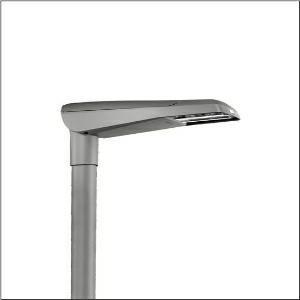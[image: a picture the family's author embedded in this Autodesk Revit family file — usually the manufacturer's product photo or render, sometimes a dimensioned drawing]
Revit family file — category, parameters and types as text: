
# Revit family: streetlight_sl_11_iq_micro___st1_2a_5xc1ac1f08de_2d80
name_source: partatom
category: Lighting Fixtures
units: mm (PartAtom-declared; Revit-internal decimal feet)

## family parameters
Cut with Voids When Loaded = No
Host = Face
Light Source = No
Part Type = Normal
Room Calculation Point = No
Round Connector Dimension = Use Diameter
Shared = No

## types (1)
- --- (1 x LED, 3860 lm, 27.4 W, 4000K)
    Apparent Load = 27 VA
    CIE Flux Codes = 33 71 96 100 100
    Color Rendering = 70
    Color Temperature = 4000K
    Default Elevation = 1800 mm
    Description = Streetlight SL 11 iQ micro, mast luminaire, primary light control with 3 zone facetted reflector, of plastic, silver coated, highly specular, primary optical cover: cover, of PMMA, transparent, light distribution: ST1.2a, light emission: direct distribution, primary light characteristic: asymmetric, installation type: post-top, side-entry, lamps: LED, High Power LED, rated values: 3.620lm | 27,7W | 130,7lm/W (begin service life); end service life: 3.620lm | 28,1W; at 50% lumin. flux: 1.810lm | 13,4W | 135,1lm/W, colour temperature: 2200/2700/3000/4000K, colour rendering: CRI > 70, light colour: 722/727/730/740, light setting 1 begin service life: 100% | 3.620lm | 27,7W | 130,7lm/W | 3.000K, light setting 1 end service life: 28,1W, further light settings possible, control: Street-Remote, Auto-Match, Temp-Guard, Lumen-Switch, Night-Set, Smart-Wire, Light-Fading, Desk-Remote (wireless, voltage-free reading and setting of iQ features in the workshop via application-optimized NFC function/RFID function), optimised constant luminous flux control (CLO 2.0), with cable H07RN-F 5x 1.5mm², mains connection: 220..240V, AC, 50/60Hz, connection cable pre-assembled, cable length: 6,5m, luminaire housing, of diecast aluminium, powder-coated, Siteco® metallic grey (DB 702S), please order mast flange separately, inclination adjustable without tools: 0°, 5°, 10°, 15° (post-top) | 0°, -5°, -10°, -15° (side-entry), sealing non-destructively replaceable, multi-level sealing system, length: 600mm, width: 174mm, height: 116mm, mast flange for spigot size: 42mm (side-entry): 5XC10008XM4, 60/48mm (side-entry/post-top): 5XC10108XM2, 76/60mm (side-entry/post-top): 5XC10108XM1, equipment: Power, protection rating (complete): IP66, insulation class (complete): insulation class II (safety insulation), certification: CE, ENEC, ENEC+, VDE, impact resistance: IK10, permissible operating ambient temperature for outdoor applications: -25..+50°C, standard-compliant lighting for roads and squares, Environmental Product Declaration (EPD) tested and certified by an independent institute, packaging unit: 1 piece

Light Distribution: ST1.2a
    Height = 116 mm
    Lamp = 1 x LED
    Lamp Light Flux = 3860 lm
    Lamp Power = 27.4 W
    Lamp count = 1
    Length = 600 mm
    Luminous efficacy = 141 lm/W
    Manufacturer = Siteco
    ModVariant = No
    Model = 5XC1AC1F08DE
    Number of Poles = 1
    OnlyDefault = Yes
    Power Factor = 1
    Product Name = Streetlight SL 11 iQ micro | ST1.2a
    Product group = mast luminaire | pylon top
    ProductGroupID = 6100
    Protection Class = Protection class II
    Protection Degree = IP 66
    RLX_Detail_Level = 1
    RLX_Emergency_Light_Flux = 0 lm
    RLX_Emergency_Type = 0
    RLX_Emergency_Type_DB = No
    RlxData = <blob elided: 59489 chars, md5=09cb2d8b>
    Socket = socket
    Standby Power = 0 W
    System Light Flux = 3860 lm
    System Power = 27 W
    Type Comments = individual setting: luminous flux: 100 % | dim-lin: 254 | 726 mA
    Type Image = l_1006566.jpg
    URL = http://relux.com
    VarID = @adj_040508
    Voltage = 0 V
    Weight = 0.00 kg
    Width = 174 mm

## geometry (parser evidence)
native form markers: Blend x4, Sweep x11
no freeform markers — native parametric forms only
